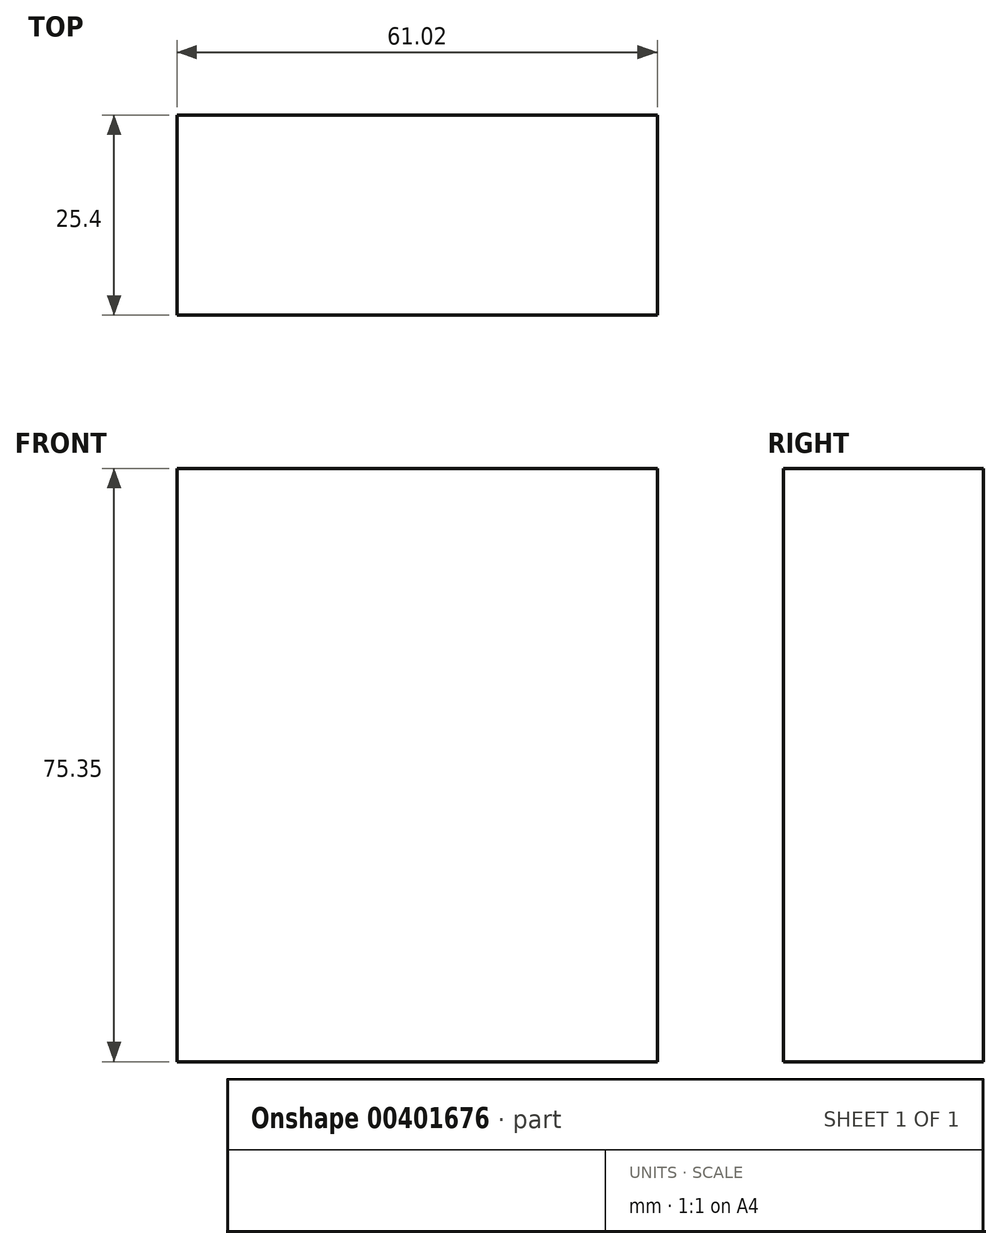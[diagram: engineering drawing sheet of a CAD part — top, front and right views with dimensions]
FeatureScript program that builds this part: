
annotation { "Feature Type Name" : "Feature", "Feature Type Description" : "" }
export const myFeature = defineFeature(function(context is Context, id is Id, definition is map)
    precondition{}
    {
        {
            var Q0;
            Q0=qCreatedBy(makeId("Front.planeOp"),FACE);
            var sketch = newSketch(context, id + "F0", { "sketchPlane" : qUnion([Q0])});
            skLineSegment(sketch, "E0.bottom", {"start": v(61.02, 50.05) * mm, "end": v(0, 50.05) * mm});
            skLineSegment(sketch, "E0.top", {"start": v(61.02, -25.3) * mm, "end": v(0, -25.3) * mm});
            skLineSegment(sketch, "E0.left", {"start": v(61.02, 50.05) * mm, "end": v(61.02, -25.3) * mm});
            skLineSegment(sketch, "E0.right", {"start": v(0, 50.05) * mm, "end": v(0, -25.3) * mm});
            skSolve(sketch);
        }
        {
            var Q0;
            Q0 = qSketchRegion(id + "F0", true);
            extrude(context, id + "F1", {"entities" : qUnion([Q0]), "depth" : 25.4 * mm});
        }
    });
